# Revit family: 210_CAD O Integral EC 45 VT
name_source: partatom
category: Mechanical Equipment
units: mm (PartAtom-declared; Revit-internal decimal feet)

## family parameters
Always vertical = Yes
Cut with Voids When Loaded = No
Part Type = Breaks Into
Room Calculation Point = No
Round Connector Dimension = Use Diameter
Shared = No
Work Plane-Based = No

## types (1)
- CAD O Integral EC 45 VT
    AA1 = 950 mm  [stored 3.1168 ft]
    AB1 = 435 mm  [stored 1.42717 ft]
    AB2 = 435 mm  [stored 1.42717 ft]
    AC1 = 915 mm  [stored 3.00197 ft]
    AC2 = 915 mm  [stored 3.00197 ft]
    BB1 = 563 mm
    BE1 = 390 mm  [stored 1.27953 ft]
    BE2 = 390 mm  [stored 1.27953 ft]
    BEXH = 310 mm
    BEXT = 310 mm
    BO1 = 390 mm  [stored 1.27953 ft]
    BOUT = 310 mm
    BS1 = 390 mm  [stored 1.27953 ft]
    BSUP = 310 mm
    CAT0 = Yes
    HEXH = 700 mm
    HEXH1 = 350 mm  [stored 1.14829 ft]
    HEXT = 700 mm
    HEXT1 = 350 mm  [stored 1.14829 ft]
    HH1 = 1530 mm  [stored 5.01969 ft]
    HH3 = 2 mm  [stored 0.00656168 ft]
    HOUT = 700 mm
    HOUT1 = 350 mm  [stored 1.14829 ft]
    HSUP = 700 mm
    HSUP1 = 350 mm  [stored 1.14829 ft]
    Manufacturer = VIM
    SP1 = 172 mm  [stored 0.564304 ft]
    SP2 = 780 mm  [stored 2.55906 ft]
    SPH1 = 720 mm  [stored 2.3622 ft]
    SPI1 = 240 mm  [stored 0.787402 ft]
    SPN = 212 mm  [stored 0.695538 ft]
    W = 500 mm
    magiPartTypeId = 210
    magiProductCode = CAD O Integral EC 45 VT
    magiProductFamilyId = CAD O Integral EC 45 VT
    magiProductId = CAD O Integral EC 45 VT

note: [stored X ft] marks values corroborated as IEEE doubles in the binary element streams (Revit-internal decimal feet)

## geometry (parser evidence)
native form markers: Sweep x2
no freeform markers — native parametric forms only
